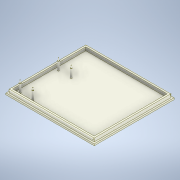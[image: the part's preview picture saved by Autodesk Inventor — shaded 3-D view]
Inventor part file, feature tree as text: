
AUTODESK INVENTOR PART (.ipt)
format: ipt  version: 2022.3 (Build 263350000, 350)  size: 185,856 bytes
history: native  units: mm
features: extrude x5, other x4, sketch x4, projected_geometry x2, folder x1, pattern_circular x1
ambient origin geometry x8: Origin, YZ Plane, XZ Plane, XY Plane, X Axis, Y Axis, Z Axis, Center Point
bodies: Body1 (feature_tree)
feature tree (17):
  other  "BARB_bottom"
  folder  "Master_XZ"
  extrude  "Floor"  Depth=2.0mm
  extrude  "Walls"  Depth=6.0mm TaperAngle=0.0deg
  other  "Lip_profile"
  extrude  "Lip"  Depth=1.0mm
  other  "Lip_edge_right"
  other  "Lip_edge_left"
  pattern_circular  "Circular Pattern1"  Count=10  [1 undecoded]
  extrude  "Standoff_base"  Depth=3.0mm TaperAngle=360.0deg
  extrude  "Standoff_tip"  Depth=95.0mm
  sketch  "Sketch3"  dims[d0=2.0mm d1=2.0mm]
  projected_geometry  "Projected Loop1"
  sketch  "Sketch4"  dims[d2=2.0mm d3=0.0mm d4=6.0mm d5=0.0mm]
  projected_geometry  "Projected Loop2"
  sketch  "Sketch6"  dims[d6=2.0mm d7=1.0mm d8=100.0mm d9=0.0mm]
  sketch  "Sketch8"  dims[d10=105.0mm d12=20.0mm d13=360.0deg d15=95.0mm d16=90.0deg d17=90.0deg d18=1.2mm d19=1.2mm d20=1.2mm d21=1.2mm d22=45.72mm d23=15.24mm d26=0.4mm d27=0.4mm d28=0.4mm d29=0.4mm d30=10.0mm d31=0.0mm d32=0.4mm d33=0.4mm d34=0.4mm d35=0.4mm d36=3.0mm d37=-0.872665mm d38=0.5mm d39=0.872665mm d40=0.5mm d41=0.872665mm]
note: 1 required parameter value undecoded (feature->parameter linkage not recoverable at this tier; creation-order binding heuristic only, values carry confidence <= 0.55)
